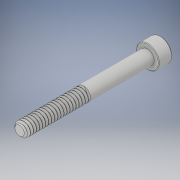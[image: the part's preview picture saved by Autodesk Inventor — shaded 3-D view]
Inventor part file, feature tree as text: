
AUTODESK INVENTOR PART (.ipt)
format: ipt  version: 2018 (Build 220112000, 112)  size: 762,880 bytes
history: native  units: in
note: dims shown in document units (in); Inventor stores cm internally (conversion verified against a paired STEP export)
features: chamfer x1
ambient origin geometry x8: Origin, YZ Plane, XZ Plane, XY Plane, X Axis, Y Axis, Z Axis, Center Point
bodies: Solid1 (feature_tree)
feature tree (1):
  chamfer  "Chamfer2"  [1 undecoded]
note: 1 required parameter value undecoded (feature->parameter linkage not recoverable at this tier; creation-order binding heuristic only, values carry confidence <= 0.55)
